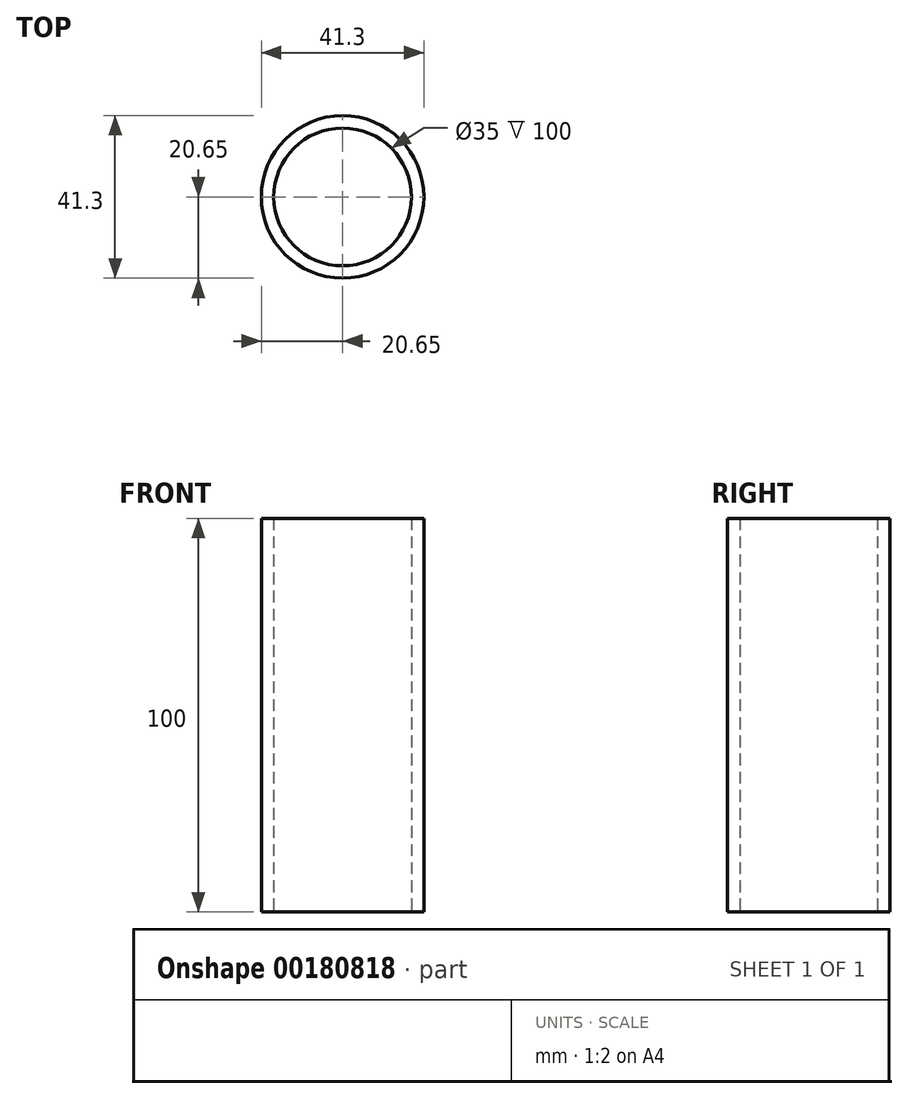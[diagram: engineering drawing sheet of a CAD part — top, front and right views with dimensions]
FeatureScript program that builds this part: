
annotation { "Feature Type Name" : "Feature", "Feature Type Description" : "" }
export const myFeature = defineFeature(function(context is Context, id is Id, definition is map)
    precondition{}
    {
        {
            var Q0;
            Q0=qCreatedBy(makeId("Top.planeOp"),FACE);
            var sketch = newSketch(context, id + "F0", { "sketchPlane" : qUnion([Q0])});
            skCircle(sketch, "E0", {"center": v(0, 0) * mm, "radius": 20.65 * mm});
            skCircle(sketch, "E1", {"center": v(0, 0) * mm, "radius": 17.5 * mm});
            skSolve(sketch);
        }
        {
            var Q0;
            Q0=makeQuery(id+"F0.imprint","IMPRINT",FACE,{"disambiguationData":[TD([[makeQuery(id+"F0.imprint","IMPRINT",EDGE,{"derivedFrom":sQuery(id+"F0.wireOp",EDGE,"E0")}),1.0]])]});
            extrude(context, id + "F1", {"entities" : qUnion([Q0]), "endBound" : BoundingType.SYMMETRIC, "depth" : 100 * mm});
        }
    });
